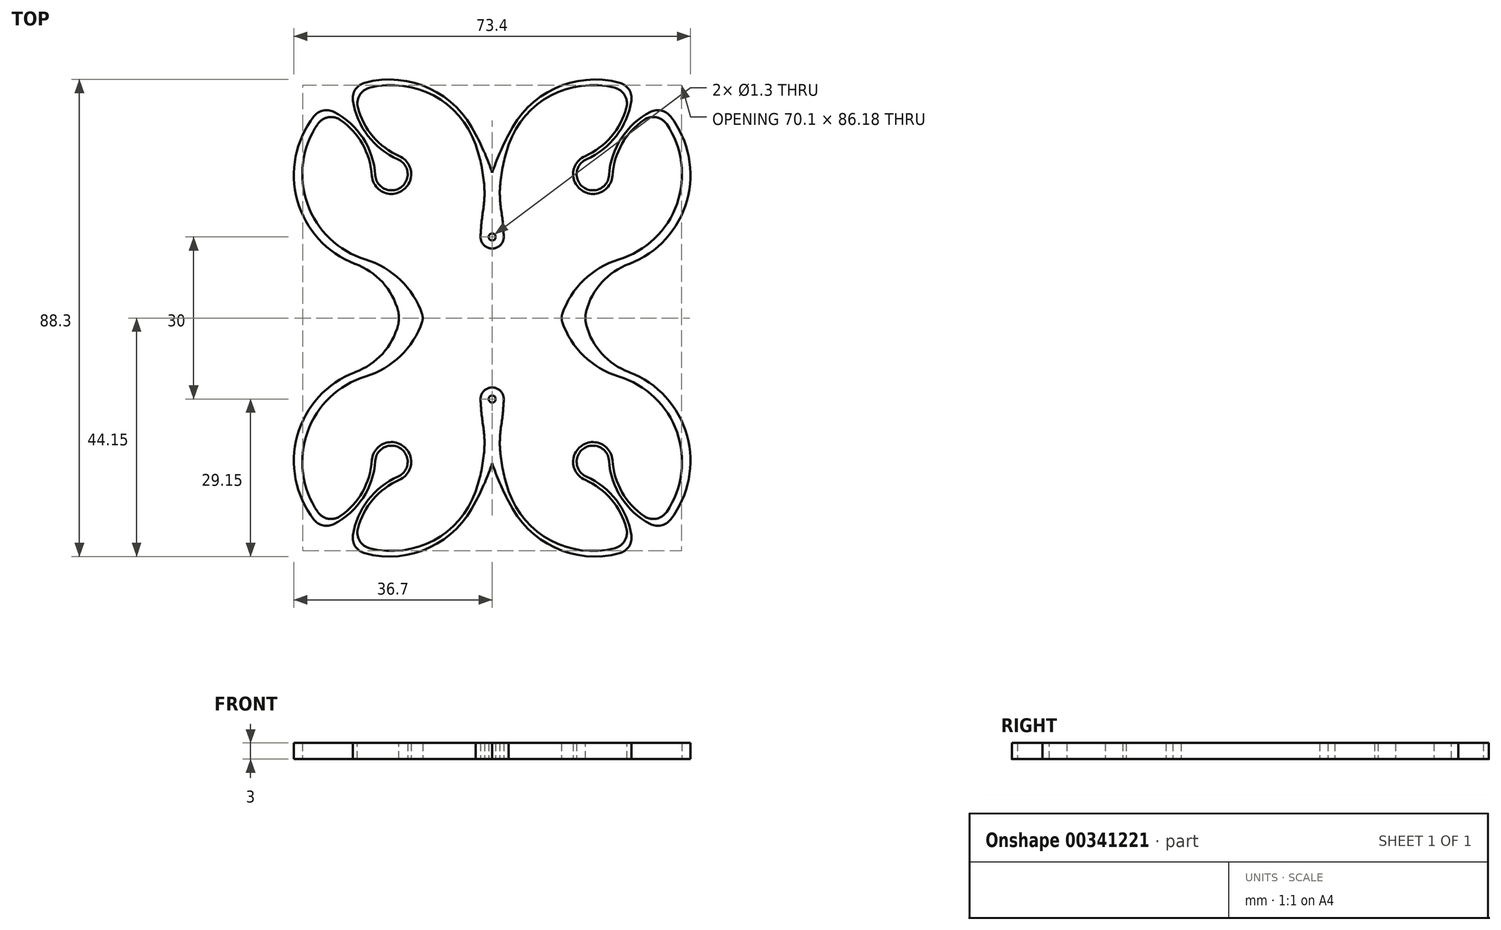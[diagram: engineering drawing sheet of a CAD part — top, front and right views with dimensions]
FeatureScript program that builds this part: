
annotation { "Feature Type Name" : "Feature", "Feature Type Description" : "" }
export const myFeature = defineFeature(function(context is Context, id is Id, definition is map)
    precondition{}
    {
        {
            var Q0;
            Q0=qCreatedBy(makeId("Top.planeOp"),FACE);
            var sketch = newSketch(context, id + "F0", { "sketchPlane" : qUnion([Q0])});
            skCircle(sketch, "E0", {"center": v(0, 0) * mm, "radius": 32.5 * mm, "construction": true});
            skCircle(sketch, "E1", {"center": v(0, 0) * mm, "radius": 15 * mm, "construction": true});
            skPoint(sketch, "E2", {"position": v(0, 15) * mm});
            skPoint(sketch, "E3", {"position": v(0, -15) * mm});
            skPoint(sketch, "E4", {"position": v(-15, 0) * mm});
            skLineSegment(sketch, "E5", {"start": v(0, 0) * mm, "end": v(27.46, 39.22) * mm, "construction": true});
            skPoint(sketch, "E6", {"position": v(18.64, 26.62) * mm});
            skCircle(sketch, "E7", {"center": v(18.64, 26.62) * mm, "radius": 15 * mm, "construction": true});
            skCircle(sketch, "E8", {"center": v(0, 15) * mm, "radius": 0.65 * mm});
            skLineSegment(sketch, "E9", {"start": v(0, 0) * mm, "end": v(11.5, 11.5) * mm, "construction": true});
            skArc(sketch, "E10.0", {"start": v(-2.15, 15.09) * mm, "mid": v(0.2, 12.86) * mm, "end": v(2.1, 15.47) * mm});
            skCircle(sketch, "E11.MirrorC", {"center": v(15, 0) * mm, "radius": 0.65 * mm});
            skArc(sketch, "E12.MirrorC", {"start": v(17.15, 0) * mm, "mid": v(14.65, -2.12) * mm, "end": v(12.96, 0.69) * mm});
            skArc(sketch, "E13", {"start": v(23.43, 10.83) * mm, "mid": v(34.6, 22.43) * mm, "end": v(30.58, 38.02) * mm});
            skArc(sketch, "E14", {"start": v(23.43, 10.83) * mm, "mid": v(16.97, 7.03) * mm, "end": v(12.96, 0.69) * mm});
            skArc(sketch, "E15", {"start": v(25.38, 10.02) * mm, "mid": v(19.89, 6.14) * mm, "end": v(17.15, 0) * mm});
            skArc(sketch, "E16", {"start": v(3.07, 32.08) * mm, "mid": v(1.42, 23.84) * mm, "end": v(2.1, 15.47) * mm});
            skArc(sketch, "E17", {"start": v(3.05, 33.94) * mm, "mid": v(-0.63, 24.81) * mm, "end": v(-2.15, 15.09) * mm});
            skArc(sketch, "E18.trimOffspring", {"start": v(25.38, 10.02) * mm, "mid": v(36.32, 22.87) * mm, "end": v(31.47, 39.04) * mm});
            skArc(sketch, "E19", {"start": v(17.44, 29.37) * mm, "mid": v(16.92, 24.16) * mm, "end": v(21.64, 26.44) * mm});
            skArc(sketch, "E20.0", {"start": v(17.18, 29.97) * mm, "mid": v(16.55, 23.63) * mm, "end": v(22.28, 26.4) * mm});
            skArc(sketch, "E21", {"start": v(30.58, 38.02) * mm, "mid": v(24.77, 33.4) * mm, "end": v(22.28, 26.4) * mm});
            skArc(sketch, "E22.0", {"start": v(31.47, 39.04) * mm, "mid": v(24.6, 34.26) * mm, "end": v(21.64, 26.44) * mm});
            skArc(sketch, "E23.MirrorCS", {"start": v(25.27, 41.73) * mm, "mid": v(22.9, 34.7) * mm, "end": v(17.18, 29.97) * mm});
            skArc(sketch, "E24.MirrorCS", {"start": v(25.92, 42.75) * mm, "mid": v(23.73, 34.76) * mm, "end": v(17.44, 29.37) * mm});
            skArc(sketch, "E25.trimOffspring", {"start": v(25.27, 41.73) * mm, "mid": v(12.06, 41.75) * mm, "end": v(3.07, 32.08) * mm});
            skArc(sketch, "E26.trimOffspring", {"start": v(25.92, 42.75) * mm, "mid": v(12.7, 42.97) * mm, "end": v(3.05, 33.94) * mm});
            skSolve(sketch);
        }
        {
            var Q0;
            Q0=makeQuery(id+"F0.imprint","IMPRINT",FACE,{"disambiguationData":[TD([[makeQuery(id+"F0.imprint","IMPRINT",EDGE,{"derivedFrom":sQuery(id+"F0.wireOp",EDGE,"E8")}),-1.0]])]});
            var Q1;
            Q1=makeQuery(id+"F0.imprint","IMPRINT",FACE,{"disambiguationData":[TD([[makeQuery(id+"F0.imprint","IMPRINT",EDGE,{"derivedFrom":sQuery(id+"F0.wireOp",EDGE,"E11.MirrorC")}),1.0]])]});
            var Q2;
            {var subQ0=sQuery(id+"F0.wireOp",EDGE,"E21");Q2=makeQuery(id+"F0.imprint","IMPRINT",FACE,{"disambiguationData":[TD([[makeQuery(id+"F0.imprint","IMPRINT",EDGE,{"derivedFrom":subQ0}),-1.0]])]});}
            var Q3;
            {var subQ0=sQuery(id+"F0.wireOp",EDGE,"E23.MirrorCS");Q3=makeQuery(id+"F0.imprint","IMPRINT",FACE,{"disambiguationData":[TD([[makeQuery(id+"F0.imprint","IMPRINT",EDGE,{"derivedFrom":subQ0}),1.0]])]});}
            var Q4;
            {var subQ5=sQuery(id+"F0.wireOp",EDGE,"E22.0");var subQ7=sQuery(id+"F0.wireOp",EDGE,"E19");var subQ8=makeQuery(id+"F0.imprint","INTERSECT",VERTEX,{"derivedFrom":[subQ7,subQ5]});Q4=makeQuery(id+"F0.imprint","IMPRINT",FACE,{"disambiguationData":[TD([[makeQuery(id+"F0.imprint","IMPRINT",EDGE,{"disambiguationData":[TD([[subQ8,1.0]])],"derivedFrom":subQ7}),-1.0]])]});}
            extrude(context, id + "F1", {"entities" : qUnion([Q0, Q1, Q2, Q3, Q4]), "depth" : 3 * mm});
        }
        {
            var Q0;
            Q0=makeQuery(id+"F1.opExtrude","SWEPT_EDGE",EDGE,{"disambiguationData":[OSD([sQuery(id+"F0.wireOp",EDGE,"E13"),sQuery(id+"F0.wireOp",EDGE,"E21")])]});
            var Q1;
            Q1=makeQuery(id+"F1.opExtrude","SWEPT_EDGE",EDGE,{"disambiguationData":[OSD([sQuery(id+"F0.wireOp",EDGE,"E13"),sQuery(id+"F0.wireOp",EDGE,"E23.MirrorCS")])]});
            var Q2;
            Q2=makeQuery(id+"F1.opExtrude","SWEPT_EDGE",EDGE,{"disambiguationData":[OSD([sQuery(id+"F0.wireOp",EDGE,"E18.trimOffspring"),sQuery(id+"F0.wireOp",EDGE,"E22.0")])]});
            var Q3;
            Q3=makeQuery(id+"F1.opExtrude","SWEPT_EDGE",EDGE,{"disambiguationData":[OSD([sQuery(id+"F0.wireOp",EDGE,"E18.trimOffspring"),sQuery(id+"F0.wireOp",EDGE,"E24.MirrorCS")])]});
            fillet(context, id + "F2", {"entities" : qUnion([Q0, Q1, Q2, Q3]), "radius" : 3 * mm, "tangentPropagation" : true, "allowEdgeOverflow" : false});
        }
        {
            var Q0;
            Q0=makeQuery(id+"F1.opExtrude","SWEPT_BODY",BODY,{"disambiguationData":[OSD([sQuery(id+"F0.wireOp",EDGE,"E8"),sQuery(id+"F0.wireOp",EDGE,"E10.0"),sQuery(id+"F0.wireOp",EDGE,"E11.MirrorC"),sQuery(id+"F0.wireOp",EDGE,"E12.MirrorC"),sQuery(id+"F0.wireOp",EDGE,"E13"),sQuery(id+"F0.wireOp",EDGE,"E14"),sQuery(id+"F0.wireOp",EDGE,"E15"),sQuery(id+"F0.wireOp",EDGE,"E16"),sQuery(id+"F0.wireOp",EDGE,"E17"),sQuery(id+"F0.wireOp",EDGE,"E18.trimOffspring"),sQuery(id+"F0.wireOp",EDGE,"E19"),sQuery(id+"F0.wireOp",EDGE,"E20.0"),sQuery(id+"F0.wireOp",EDGE,"E21"),sQuery(id+"F0.wireOp",EDGE,"E22.0"),sQuery(id+"F0.wireOp",EDGE,"E23.MirrorCS"),sQuery(id+"F0.wireOp",EDGE,"E24.MirrorCS")])]});
            var Q1;
            Q1=qCreatedBy(makeId("Right.planeOp"),FACE);
            mirror(context, id + "F3", {"operationType" : NewBodyOperationType.ADD, "entities" : qUnion([Q0]), "mirrorPlane" : qUnion([Q1])});
        }
        {
            var Q0;
            Q0=makeQuery(id+"F3.boolean.opBoolean","INTERSECT",EDGE,{"derivedFrom":[makeQuery(id+"F1.opExtrude","SWEPT_FACE",FACE,{"disambiguationData":[OSD([sQuery(id+"F0.wireOp",EDGE,"E17")])]}),makeQuery(id+"F3.opPattern","COPY",FACE,{"derivedFrom":makeQuery(id+"F1.opExtrude","SWEPT_FACE",FACE,{"disambiguationData":[OSD([sQuery(id+"F0.wireOp",EDGE,"E16")])]}),"instanceName":"1"})]});
            var Q1;
            Q1=makeQuery(id+"F3.boolean.opBoolean","INTERSECT",EDGE,{"derivedFrom":[makeQuery(id+"F1.opExtrude","SWEPT_FACE",FACE,{"disambiguationData":[OSD([sQuery(id+"F0.wireOp",EDGE,"E16")])]}),makeQuery(id+"F3.opPattern","COPY",FACE,{"derivedFrom":makeQuery(id+"F1.opExtrude","SWEPT_FACE",FACE,{"disambiguationData":[OSD([sQuery(id+"F0.wireOp",EDGE,"E17")])]}),"instanceName":"1"})]});
            fillet(context, id + "F4", {"entities" : qUnion([Q0, Q1]), "radius" : 20 * mm, "tangentPropagation" : true, "allowEdgeOverflow" : false});
        }
        {
            var Q0;
            Q0=makeQuery(id+"F1.opExtrude","SWEPT_BODY",BODY,{"disambiguationData":[OSD([sQuery(id+"F0.wireOp",EDGE,"E8"),sQuery(id+"F0.wireOp",EDGE,"E10.0"),sQuery(id+"F0.wireOp",EDGE,"E11.MirrorC"),sQuery(id+"F0.wireOp",EDGE,"E12.MirrorC"),sQuery(id+"F0.wireOp",EDGE,"E13"),sQuery(id+"F0.wireOp",EDGE,"E14"),sQuery(id+"F0.wireOp",EDGE,"E15"),sQuery(id+"F0.wireOp",EDGE,"E16"),sQuery(id+"F0.wireOp",EDGE,"E17"),sQuery(id+"F0.wireOp",EDGE,"E18.trimOffspring"),sQuery(id+"F0.wireOp",EDGE,"E19"),sQuery(id+"F0.wireOp",EDGE,"E20.0"),sQuery(id+"F0.wireOp",EDGE,"E21"),sQuery(id+"F0.wireOp",EDGE,"E22.0"),sQuery(id+"F0.wireOp",EDGE,"E23.MirrorCS"),sQuery(id+"F0.wireOp",EDGE,"E24.MirrorCS")])]});
            var Q1;
            Q1=qCreatedBy(makeId("Front.planeOp"),FACE);
            mirror(context, id + "F5", {"operationType" : NewBodyOperationType.ADD, "entities" : qUnion([Q0]), "mirrorPlane" : qUnion([Q1])});
        }
        {
            var Q0;
            {var subQ0=makeQuery(id+"F1.opExtrude","SWEPT_EDGE",EDGE,{"disambiguationData":[OSD([sQuery(id+"F0.wireOp",EDGE,"E12.MirrorC"),sQuery(id+"F0.wireOp",EDGE,"E15")])]});Q0=makeQuery(id+"F5.boolean.opBoolean","MERGE",EDGE,{"derivedFrom":[subQ0,makeQuery(id+"F5.opPattern","COPY",EDGE,{"derivedFrom":subQ0,"instanceName":"1"})]});}
            var Q1;
            {var subQ0=makeQuery(id+"F3.opPattern","COPY",EDGE,{"derivedFrom":makeQuery(id+"F1.opExtrude","SWEPT_EDGE",EDGE,{"disambiguationData":[OSD([sQuery(id+"F0.wireOp",EDGE,"E12.MirrorC"),sQuery(id+"F0.wireOp",EDGE,"E15")])]}),"instanceName":"1"});Q1=makeQuery(id+"F5.boolean.opBoolean","MERGE",EDGE,{"derivedFrom":[subQ0,makeQuery(id+"F5.opPattern","COPY",EDGE,{"derivedFrom":subQ0,"instanceName":"1"})]});}
            fillet(context, id + "F6", {"entities" : qUnion([Q0, Q1]), "radius" : 5 * mm, "tangentPropagation" : true, "allowEdgeOverflow" : false});
        }
    });
